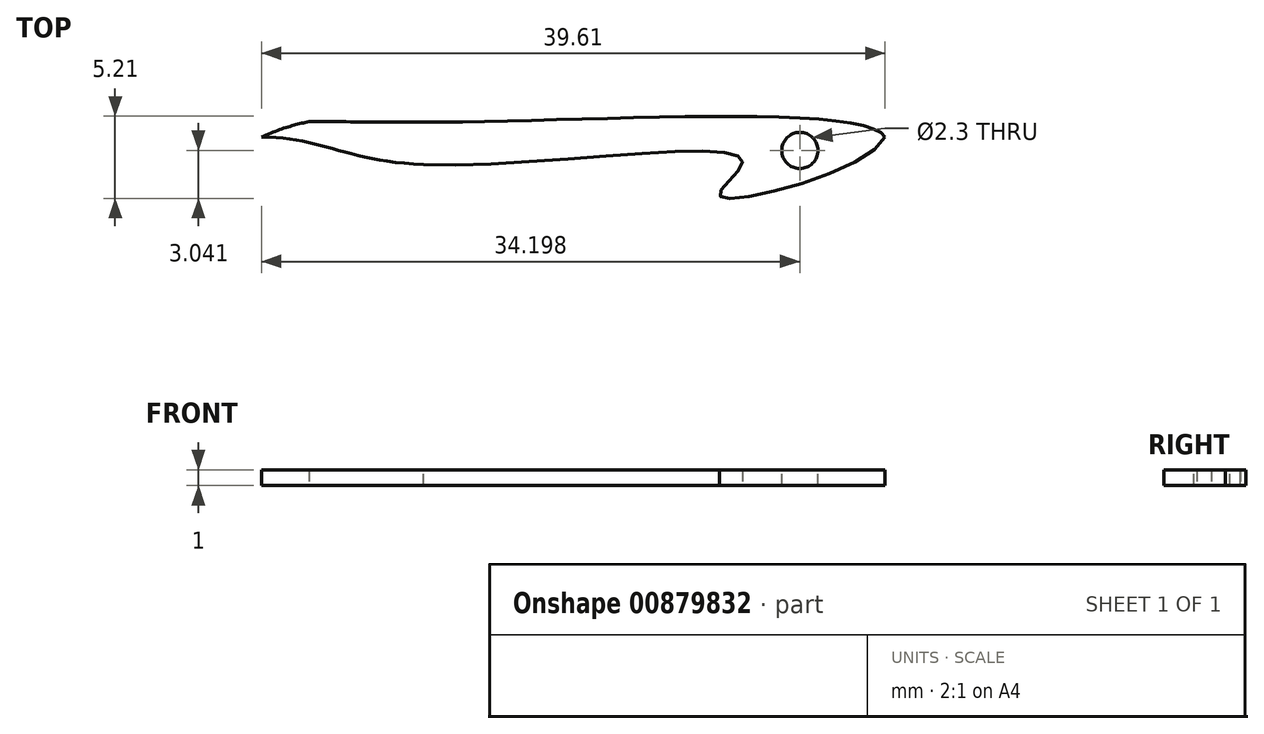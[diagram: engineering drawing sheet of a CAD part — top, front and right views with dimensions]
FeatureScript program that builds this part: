
annotation { "Feature Type Name" : "Feature", "Feature Type Description" : "" }
export const myFeature = defineFeature(function(context is Context, id is Id, definition is map)
    precondition{}
    {
        {
            var Q0;
            Q0=qCreatedBy(makeId("Top.planeOp"),FACE);
            var sketch = newSketch(context, id + "F0", { "sketchPlane" : qUnion([Q0])});
            skLineSegment(sketch, "E0", {"start": v(0, 0) * mm, "end": v(29.32, 0) * mm});
            skFitSpline(sketch, "E1", {"points": [v(-10.29, 0) * mm, v(0, 0.96) * mm, v(29.32, 0) * mm], "startDerivative": vector(30.44, 13.45) * mm, "endDerivative": vector(6.43, -11.12) * mm});
            skFitSpline(sketch, "E2", {"points": [v(-10.29, 0) * mm, v(0, -1.75) * mm, v(20.27, -1.57) * mm, v(18.82, -3.73) * mm, v(29.32, 0) * mm], "startDerivative": vector(44.51, 0) * mm, "endDerivative": vector(10.8, 24.49) * mm});
            skLineSegment(sketch, "E3.MirrorCS", {"start": v(0, 0) * mm, "end": v(15.74, 0) * mm});
            skPoint(sketch, "E4", {"position": v(0, 0) * mm});
            skPoint(sketch, "E5.MirrorCS.start.orphan", {"position": v(0, -2.43) * mm});
            skFitSpline(sketch, "E6", {"points": [v(0, 0.96) * mm, v(-8.18, 0.96) * mm, v(-22.18, 0) * mm, v(-28.72, 0) * mm, v(-27.42, 1.15) * mm, v(-32.1, 0) * mm, v(-23.06, -1.97) * mm, v(-16.3, -2.17) * mm, v(0, -1.75) * mm], "startDerivative": vector(-80.72, -1.28) * mm, "endDerivative": vector(63.05, 6.49) * mm});
            skSolve(sketch);
        }
        {
            var Q0;
            Q0=makeQuery(id+"F0.imprint","IMPRINT",FACE,{"disambiguationData":[TD([[makeQuery(id+"F0.imprint","IMPRINT",EDGE,{"derivedFrom":sQuery(id+"F0.wireOp",EDGE,"E1")}),-1.0]])]});
            extrude(context, id + "F1", {"entities" : qUnion([Q0]), "depth" : 1 * mm, "offsetDistance" : 25 * mm});
        }
        {
            var Q0;
            Q0=makeQuery(id+"F1.opExtrude","CAP_FACE",FACE,{"disambiguationData":[OSD([sQuery(id+"F0.wireOp",EDGE,"E1"),sQuery(id+"F0.wireOp",EDGE,"E2"),sQuery(id+"F0.wireOp",EDGE,"E6")])],"isStart":false});
            var sketch = newSketch(context, id + "F2", { "sketchPlane" : qUnion([Q0])});
            skCircle(sketch, "E7", {"center": v(23.9, -0.85) * mm, "radius": 1.15 * mm});
            skSolve(sketch);
        }
        {
            var Q0;
            Q0=makeQuery(id+"F2.imprint","IMPRINT",FACE,{"disambiguationData":[TD([[makeQuery(id+"F2.imprint","IMPRINT",EDGE,{"derivedFrom":sQuery(id+"F2.wireOp",EDGE,"E7")}),1.0]])]});
            extrude(context, id + "F3", {"entities" : qUnion([Q0]), "operationType" : NewBodyOperationType.REMOVE, "oppositeDirection" : true, "depth" : 25 * mm, "offsetDistance" : 25 * mm});
        }
    });
